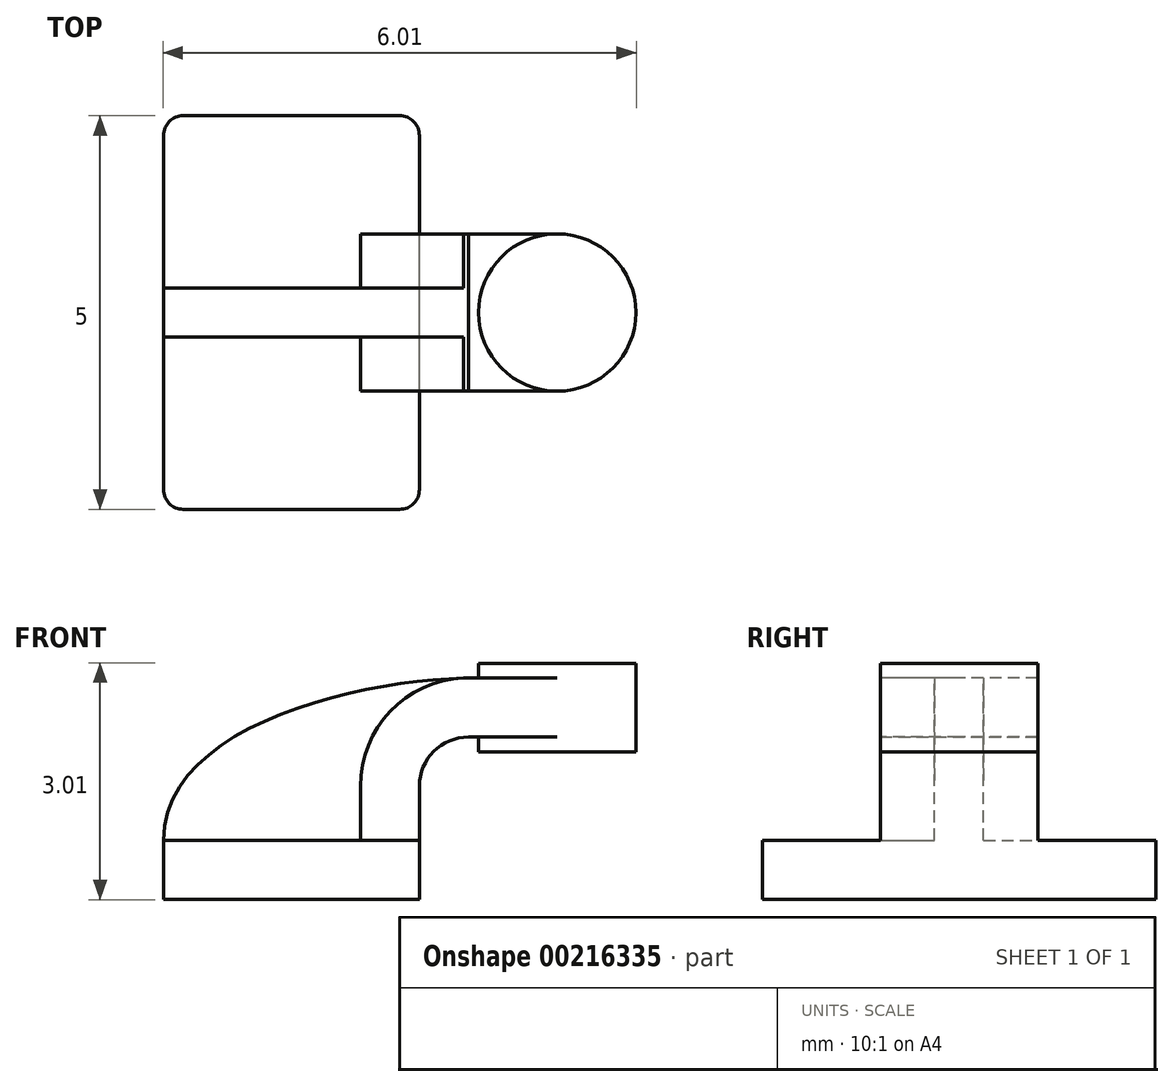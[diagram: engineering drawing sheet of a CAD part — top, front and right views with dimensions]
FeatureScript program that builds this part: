
annotation { "Feature Type Name" : "Feature", "Feature Type Description" : "" }
export const myFeature = defineFeature(function(context is Context, id is Id, definition is map)
    precondition{}
    {
        {
            var Q0;
            Q0=qCreatedBy(makeId("Front.planeOp"),FACE);
            var sketch = newSketch(context, id + "F0", { "sketchPlane" : qUnion([Q0])});
            skLineSegment(sketch, "E0.bottom", {"start": v(1.63, -0.37) * mm, "end": v(-1.62, -0.37) * mm});
            skLineSegment(sketch, "E0.top", {"start": v(1.62, 0.38) * mm, "end": v(-1.62, 0.38) * mm});
            skLineSegment(sketch, "E0.left", {"start": v(1.63, -0.37) * mm, "end": v(1.63, 0.38) * mm});
            skLineSegment(sketch, "E0.right", {"start": v(-1.62, -0.37) * mm, "end": v(-1.62, 0.38) * mm});
            skPoint(sketch, "E0.middle", {"position": v(0, 0) * mm});
            skLineSegment(sketch, "E1.bottom", {"start": v(4.37, 1.5) * mm, "end": v(2.37, 1.5) * mm});
            skLineSegment(sketch, "E1.top", {"start": v(4.37, 2.63) * mm, "end": v(2.37, 2.63) * mm});
            skLineSegment(sketch, "E1.left", {"start": v(4.37, 1.5) * mm, "end": v(4.37, 2.63) * mm});
            skLineSegment(sketch, "E1.right", {"start": v(2.37, 1.5) * mm, "end": v(2.37, 2.63) * mm});
            skPoint(sketch, "E1.middle", {"position": v(3.37, 2.06) * mm});
            skLineSegment(sketch, "E2", {"start": v(1.62, 0.38) * mm, "end": v(1.62, 1.06) * mm});
            skArc(sketch, "E3", {"start": v(1.62, 1.06) * mm, "mid": v(1.8, 1.5) * mm, "end": v(2.25, 1.69) * mm});
            skLineSegment(sketch, "E4", {"start": v(2.25, 1.69) * mm, "end": v(3.37, 1.69) * mm});
            skLineSegment(sketch, "E5.0", {"start": v(2.25, 2.44) * mm, "end": v(3.37, 2.44) * mm});
            skArc(sketch, "E5.1", {"start": v(0.87, 1.06) * mm, "mid": v(1.28, 2.04) * mm, "end": v(2.25, 2.44) * mm});
            skLineSegment(sketch, "E5.2", {"start": v(0.87, 0.38) * mm, "end": v(0.87, 1.06) * mm});
            skLineSegment(sketch, "E6", {"start": v(3.37, 1.5) * mm, "end": v(3.37, 2.63) * mm});
            skFitSpline(sketch, "E7", {"points": [v(-1.63, 0.38) * mm, v(2.25, 2.44) * mm], "startDerivative": vector(0.01, 4.4) * mm, "endDerivative": vector(4.15, 0.07) * mm});
            skSolve(sketch);
        }
        {
            var Q0;
            Q0=makeQuery(id+"F0.imprint","IMPRINT",FACE,{"disambiguationData":[TD([[makeQuery(id+"F0.imprint","IMPRINT",EDGE,{"derivedFrom":sQuery(id+"F0.wireOp",EDGE,"E0.bottom")}),-1.0]])]});
            extrude(context, id + "F1", {"entities" : qUnion([Q0]), "endBound" : BoundingType.SYMMETRIC, "depth" : 5 * mm});
        }
        {
            var Q0;
            {var subQ1=sQuery(id+"F0.wireOp",EDGE,"E2");Q0=makeQuery(id+"F0.imprint","IMPRINT",FACE,{"disambiguationData":[TD([[makeQuery(id+"F0.imprint","IMPRINT",EDGE,{"derivedFrom":subQ1}),1.0]])]});}
            var Q1;
            {var subQ0=sQuery(id+"F0.wireOp",EDGE,"E4");var subQ1=sQuery(id+"F0.wireOp",EDGE,"E1.right");var subQ2=makeQuery(id+"F0.imprint","INTERSECT",VERTEX,{"derivedFrom":[subQ1,subQ0]});Q1=makeQuery(id+"F0.imprint","IMPRINT",FACE,{"disambiguationData":[TD([[makeQuery(id+"F0.imprint","IMPRINT",EDGE,{"disambiguationData":[TD([[subQ2,-1.0]])],"derivedFrom":subQ1}),-1.0]])]});}
            extrude(context, id + "F2", {"entities" : qUnion([Q0, Q1]), "operationType" : NewBodyOperationType.ADD, "endBound" : BoundingType.SYMMETRIC, "depth" : 2 * mm});
        }
        {
            var Q0;
            {var subQ3=sQuery(id+"F0.wireOp",EDGE,"E5.2");Q0=makeQuery(id+"F0.imprint","IMPRINT",FACE,{"disambiguationData":[TD([[makeQuery(id+"F0.imprint","IMPRINT",EDGE,{"derivedFrom":subQ3}),1.0]])]});}
            extrude(context, id + "F3", {"entities" : qUnion([Q0]), "operationType" : NewBodyOperationType.ADD, "endBound" : BoundingType.SYMMETRIC, "depth" : .625 * mm});
        }
        {
            var Q0;
            {var subQ0=sQuery(id+"F0.wireOp",EDGE,"E1.left");Q0=makeQuery(id+"F0.imprint","IMPRINT",FACE,{"disambiguationData":[TD([[makeQuery(id+"F0.imprint","IMPRINT",EDGE,{"derivedFrom":subQ0}),1.0]])]});}
            var Q1;
            Q1=sQuery(id+"F0.wireOp",EDGE,"E6");
            revolve(context, id + "F4", {"operationType" : NewBodyOperationType.ADD, "entities" : qUnion([Q0]), "axis" : qUnion([Q1]), "revolveType" : RevolveType.FULL});
        }
        {
            var Q0;
            Q0=makeQuery(id+"F1.opExtrude","CAP_EDGE",EDGE,{"disambiguationData":[OSD([sQuery(id+"F0.wireOp",EDGE,"E0.left")])],"isStart":false});
            var Q1;
            Q1=makeQuery(id+"F1.opExtrude","CAP_EDGE",EDGE,{"disambiguationData":[OSD([sQuery(id+"F0.wireOp",EDGE,"E0.right")])],"isStart":false});
            var Q2;
            Q2=makeQuery(id+"F1.opExtrude","CAP_EDGE",EDGE,{"disambiguationData":[OSD([sQuery(id+"F0.wireOp",EDGE,"E0.left")])],"isStart":true});
            var Q3;
            Q3=makeQuery(id+"F1.opExtrude","CAP_EDGE",EDGE,{"disambiguationData":[OSD([sQuery(id+"F0.wireOp",EDGE,"E0.right")])],"isStart":true});
            fillet(context, id + "F5", {"entities" : qUnion([Q0, Q1, Q2, Q3]), "radius" : .25 * mm, "tangentPropagation" : true, "allowEdgeOverflow" : false});
        }
    });
